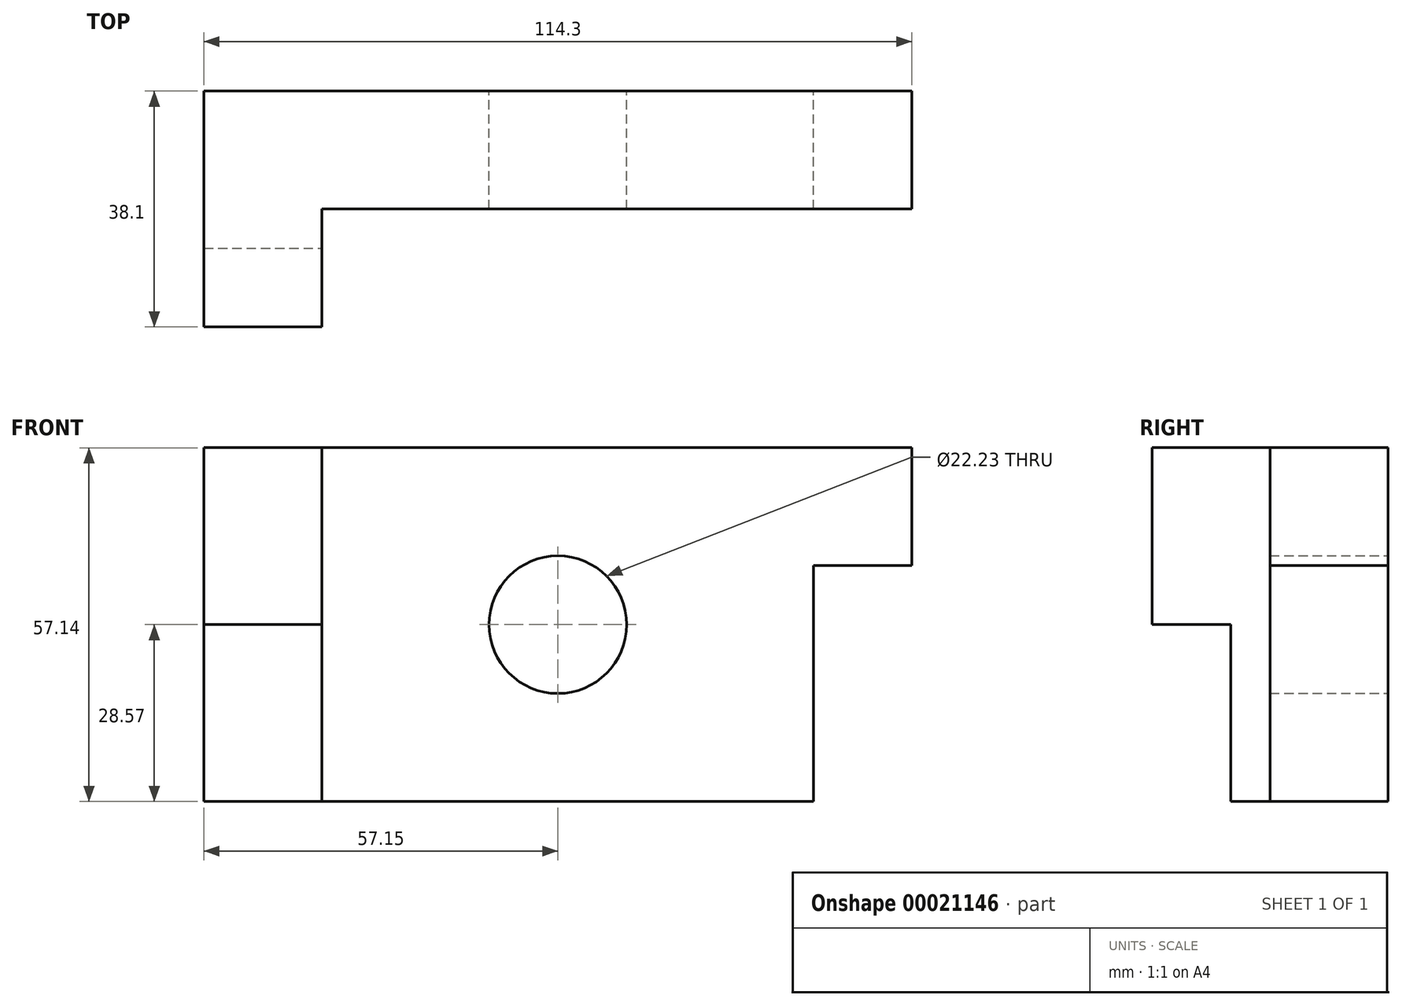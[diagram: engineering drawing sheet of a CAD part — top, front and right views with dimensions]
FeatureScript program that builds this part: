
annotation { "Feature Type Name" : "Feature", "Feature Type Description" : "" }
export const myFeature = defineFeature(function(context is Context, id is Id, definition is map)
    precondition{}
    {
        {
            var Q0;
            Q0=qCreatedBy(makeId("Front.planeOp"),FACE);
            var sketch = newSketch(context, id + "F0", { "sketchPlane" : qUnion([Q0])});
            skCircle(sketch, "E0", {"center": v(0, 0) * mm, "radius": 11.11 * mm});
            skLineSegment(sketch, "E1.rect.bottom", {"start": v(-57.15, 28.57) * mm, "end": v(57.15, 28.57) * mm});
            skLineSegment(sketch, "E1.rect.top", {"start": v(-57.15, -28.57) * mm, "end": v(57.15, -28.57) * mm});
            skLineSegment(sketch, "E1.rect.left", {"start": v(-57.15, 28.57) * mm, "end": v(-57.15, -28.57) * mm});
            skLineSegment(sketch, "E1.rect.right", {"start": v(57.15, 28.57) * mm, "end": v(57.15, -28.57) * mm});
            skLineSegment(sketch, "E2.bottom", {"start": v(57.15, -28.57) * mm, "end": v(41.27, -28.57) * mm});
            skLineSegment(sketch, "E2.top", {"start": v(57.15, 9.53) * mm, "end": v(41.27, 9.53) * mm});
            skLineSegment(sketch, "E2.left", {"start": v(57.15, -28.57) * mm, "end": v(57.15, 9.53) * mm});
            skLineSegment(sketch, "E2.right", {"start": v(41.27, -28.57) * mm, "end": v(41.27, 9.53) * mm});
            skSolve(sketch);
        }
        {
            var Q0;
            Q0=makeQuery(id+"F0.imprint","IMPRINT",FACE,{"disambiguationData":[TD([[makeQuery(id+"F0.imprint","IMPRINT",EDGE,{"derivedFrom":sQuery(id+"F0.wireOp",EDGE,"E0")}),-1.0]])]});
            extrude(context, id + "F1", {"entities" : qUnion([Q0]), "depth" : 19.05 * mm});
        }
        {
            var Q0;
            Q0=makeQuery(id+"F1.opExtrude","CAP_FACE",FACE,{"disambiguationData":[OSD([sQuery(id+"F0.wireOp",EDGE,"E0"),sQuery(id+"F0.wireOp",EDGE,"E1.rect.bottom"),sQuery(id+"F0.wireOp",EDGE,"E1.rect.top"),sQuery(id+"F0.wireOp",EDGE,"E1.rect.left"),sQuery(id+"F0.wireOp",EDGE,"E1.rect.right"),sQuery(id+"F0.wireOp",EDGE,"E2.top"),sQuery(id+"F0.wireOp",EDGE,"E2.right")])],"isStart":false});
            var sketch = newSketch(context, id + "F2", { "sketchPlane" : qUnion([Q0])});
            skLineSegment(sketch, "E3.bottom", {"start": v(-57.15, 28.57) * mm, "end": v(-38.1, 28.57) * mm});
            skLineSegment(sketch, "E3.top", {"start": v(-57.15, -28.57) * mm, "end": v(-38.1, -28.57) * mm});
            skLineSegment(sketch, "E3.left", {"start": v(-57.15, 28.57) * mm, "end": v(-57.15, -28.57) * mm});
            skLineSegment(sketch, "E3.right", {"start": v(-38.1, 28.57) * mm, "end": v(-38.1, -28.57) * mm});
            skSolve(sketch);
        }
        {
            var Q0;
            Q0 = qSketchRegion(id + "F2", true);
            extrude(context, id + "F3", {"entities" : qUnion([Q0]), "operationType" : NewBodyOperationType.ADD, "depth" : 6.35 * mm});
        }
        {
            var Q0;
            Q0=makeQuery(id+"F3.opExtrude","CAP_FACE",FACE,{"disambiguationData":[OSD([sQuery(id+"F2.wireOp",EDGE,"E3.bottom"),sQuery(id+"F2.wireOp",EDGE,"E3.top"),sQuery(id+"F2.wireOp",EDGE,"E3.left"),sQuery(id+"F2.wireOp",EDGE,"E3.right")])],"isStart":false});
            var sketch = newSketch(context, id + "F4", { "sketchPlane" : qUnion([Q0])});
            skLineSegment(sketch, "E4.bottom", {"start": v(-57.15, 28.57) * mm, "end": v(-38.1, 28.57) * mm});
            skLineSegment(sketch, "E4.top", {"start": v(-57.15, 0) * mm, "end": v(-38.1, 0) * mm});
            skLineSegment(sketch, "E4.left", {"start": v(-57.15, 28.57) * mm, "end": v(-57.15, 0) * mm});
            skLineSegment(sketch, "E4.right", {"start": v(-38.1, 28.57) * mm, "end": v(-38.1, 0) * mm});
            skSolve(sketch);
        }
        {
            var Q0;
            Q0 = qSketchRegion(id + "F4", true);
            extrude(context, id + "F5", {"entities" : qUnion([Q0]), "operationType" : NewBodyOperationType.ADD, "depth" : 12.7 * mm});
        }
    });
